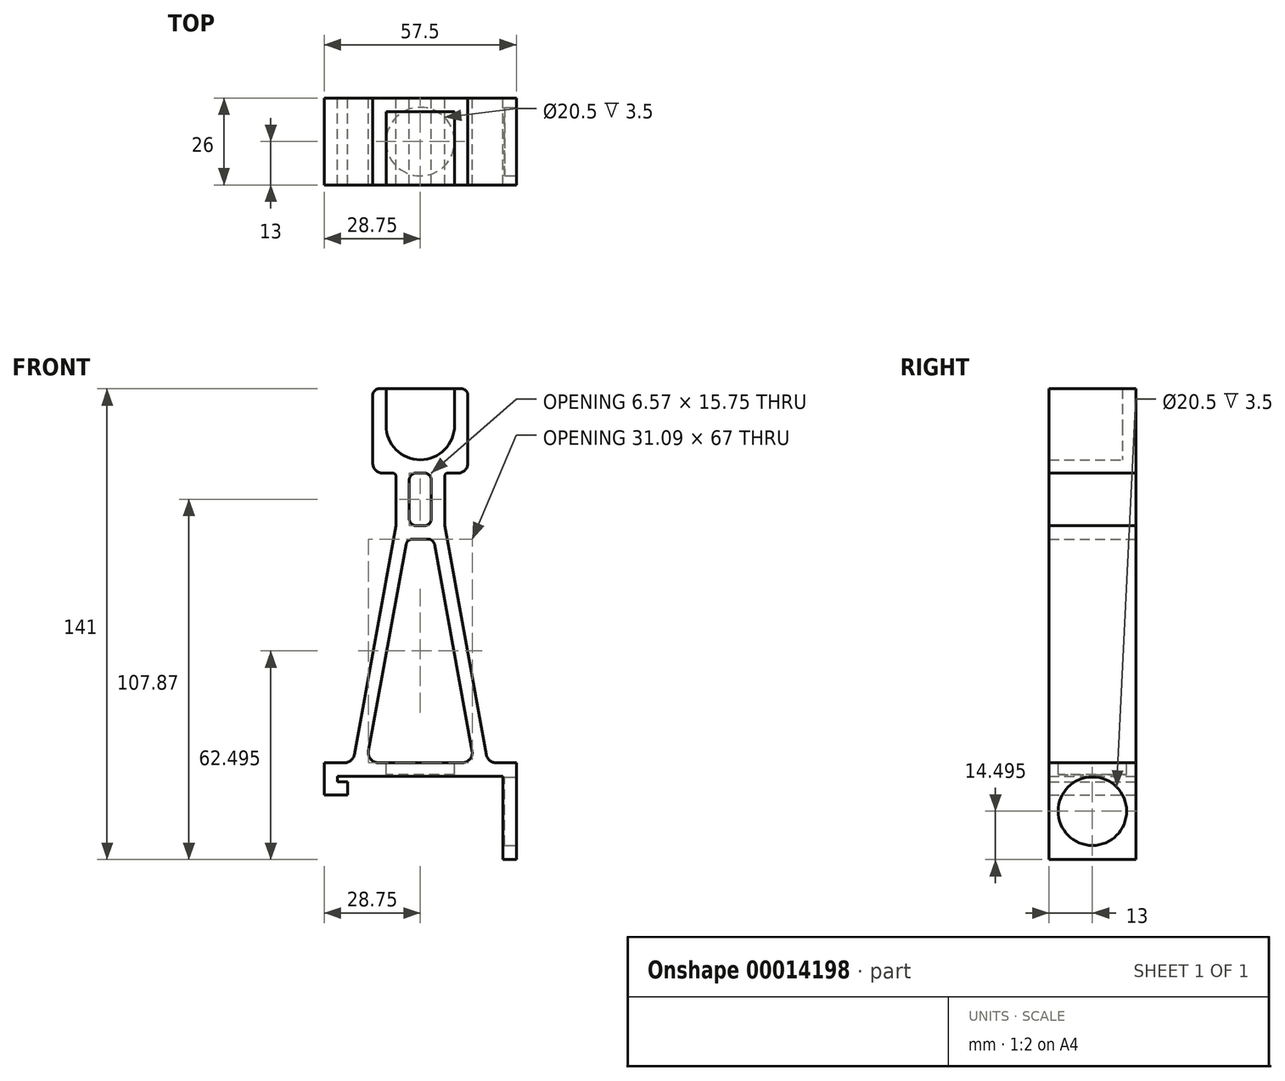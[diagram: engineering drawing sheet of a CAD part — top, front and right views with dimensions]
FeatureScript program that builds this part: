
annotation { "Feature Type Name" : "Feature", "Feature Type Description" : "" }
export const myFeature = defineFeature(function(context is Context, id is Id, definition is map)
    precondition{}
    {
        {
            var Q0;
            Q0=qCreatedBy(makeId("Front.planeOp"),FACE);
            var sketch = newSketch(context, id + "F0", { "sketchPlane" : qUnion([Q0])});
            skLineSegment(sketch, "E0", {"start": v(-28.75, 2.04) * mm, "end": v(-22.71, 2.04) * mm});
            skLineSegment(sketch, "E1", {"start": v(28.75, 2.04) * mm, "end": v(28.75, -26.96) * mm});
            skLineSegment(sketch, "E2", {"start": v(28.75, -26.96) * mm, "end": v(24.75, -26.96) * mm});
            skLineSegment(sketch, "E3", {"start": v(24.75, -26.96) * mm, "end": v(24.75, -1.96) * mm});
            skLineSegment(sketch, "E4", {"start": v(24.75, -1.96) * mm, "end": v(-24.75, -1.96) * mm});
            skLineSegment(sketch, "E5", {"start": v(-24.75, -1.96) * mm, "end": v(-24.75, -3.66) * mm});
            skLineSegment(sketch, "E6", {"start": v(-24.75, -3.66) * mm, "end": v(-21.75, -3.66) * mm});
            skLineSegment(sketch, "E7", {"start": v(-21.75, -3.66) * mm, "end": v(-21.75, -7.66) * mm});
            skLineSegment(sketch, "E8", {"start": v(-21.75, -7.66) * mm, "end": v(-28.75, -7.66) * mm});
            skLineSegment(sketch, "E9", {"start": v(-28.75, -7.66) * mm, "end": v(-28.75, 2.04) * mm});
            skLineSegment(sketch, "E10", {"start": v(-19.76, 4.5) * mm, "end": v(-7.29, 73.04) * mm});
            skLineSegment(sketch, "E11", {"start": v(-1.29, 73.04) * mm, "end": v(1.29, 73.04) * mm});
            skLineSegment(sketch, "E12", {"start": v(7.29, 73.04) * mm, "end": v(19.76, 4.5) * mm});
            skLineSegment(sketch, "E13", {"start": v(-15.5, 5.57) * mm, "end": v(-4.25, 67.4) * mm});
            skLineSegment(sketch, "E14", {"start": v(-2.28, 69.04) * mm, "end": v(2.28, 69.04) * mm});
            skLineSegment(sketch, "E15", {"start": v(4.25, 67.4) * mm, "end": v(15.5, 5.57) * mm});
            skLineSegment(sketch, "E16.trimOffspring", {"start": v(-12.55, 2.04) * mm, "end": v(12.55, 2.04) * mm});
            skLineSegment(sketch, "E17.trimOffspring", {"start": v(22.71, 2.04) * mm, "end": v(28.75, 2.04) * mm});
            skLineSegment(sketch, "E18", {"start": v(-7.29, 73.04) * mm, "end": v(-7.29, 87.79) * mm});
            skLineSegment(sketch, "E19", {"start": v(7.29, 87.79) * mm, "end": v(7.29, 73.04) * mm});
            skLineSegment(sketch, "E20", {"start": v(-3.29, 75.04) * mm, "end": v(-3.29, 86.79) * mm});
            skLineSegment(sketch, "E21", {"start": v(3.29, 86.79) * mm, "end": v(3.29, 75.04) * mm});
            skArc(sketch, "E22", {"start": v(-10.25, 103.04) * mm, "mid": v(0, 92.79) * mm, "end": v(10.25, 103.04) * mm});
            skPoint(sketch, "E22.centerSnap0", {"position": v(0, 73.04) * mm});
            skLineSegment(sketch, "E23", {"start": v(-10.25, 114.04) * mm, "end": v(-10.25, 103.04) * mm});
            skLineSegment(sketch, "E24", {"start": v(10.25, 114.04) * mm, "end": v(10.25, 103.04) * mm});
            skLineSegment(sketch, "E25", {"start": v(-10.25, 114.04) * mm, "end": v(-12.25, 114.04) * mm});
            skLineSegment(sketch, "E26", {"start": v(-14.25, 112.04) * mm, "end": v(-14.25, 91.79) * mm});
            skLineSegment(sketch, "E27", {"start": v(-11.25, 88.79) * mm, "end": v(-8.29, 88.79) * mm});
            skLineSegment(sketch, "E28", {"start": v(14.25, 91.79) * mm, "end": v(14.25, 112.04) * mm});
            skLineSegment(sketch, "E29", {"start": v(12.25, 114.04) * mm, "end": v(10.25, 114.04) * mm});
            skLineSegment(sketch, "E30.trimOffspring", {"start": v(-1.29, 88.79) * mm, "end": v(1.29, 88.79) * mm});
            skLineSegment(sketch, "E31.trimOffspring", {"start": v(8.29, 88.79) * mm, "end": v(11.25, 88.79) * mm});
            skLineSegment(sketch, "E32", {"start": v(-10.25, 114.04) * mm, "end": v(10.25, 114.04) * mm});
            skPoint(sketch, "E33.visualSharp", {"position": v(-14.25, 88.79) * mm});
            skArc(sketch, "E33.filletArc", {"start": v(-14.25, 91.79) * mm, "mid": v(-13.37, 89.66) * mm, "end": v(-11.25, 88.79) * mm});
            skPoint(sketch, "E34.visualSharp", {"position": v(14.25, 88.79) * mm});
            skArc(sketch, "E34.filletArc", {"start": v(11.25, 88.79) * mm, "mid": v(13.37, 89.66) * mm, "end": v(14.25, 91.79) * mm});
            skPoint(sketch, "E35.visualSharp", {"position": v(14.25, 114.04) * mm});
            skArc(sketch, "E35.filletArc", {"start": v(14.25, 112.04) * mm, "mid": v(13.66, 113.45) * mm, "end": v(12.25, 114.04) * mm});
            skPoint(sketch, "E36.visualSharp", {"position": v(-14.25, 114.04) * mm});
            skArc(sketch, "E36.filletArc", {"start": v(-12.25, 114.04) * mm, "mid": v(-13.66, 113.45) * mm, "end": v(-14.25, 112.04) * mm});
            skPoint(sketch, "E37.visualSharp", {"position": v(-7.29, 88.79) * mm});
            skArc(sketch, "E37.filletArc", {"start": v(-7.29, 87.79) * mm, "mid": v(-7.58, 88.5) * mm, "end": v(-8.29, 88.79) * mm});
            skPoint(sketch, "E38.visualSharp", {"position": v(7.29, 88.79) * mm});
            skArc(sketch, "E38.filletArc", {"start": v(8.29, 88.79) * mm, "mid": v(7.58, 88.5) * mm, "end": v(7.29, 87.79) * mm});
            skPoint(sketch, "E39.visualSharp", {"position": v(-3.29, 88.79) * mm});
            skArc(sketch, "E39.filletArc", {"start": v(-1.29, 88.79) * mm, "mid": v(-2.7, 88.2) * mm, "end": v(-3.29, 86.79) * mm});
            skPoint(sketch, "E40.visualSharp", {"position": v(3.29, 88.79) * mm});
            skArc(sketch, "E40.filletArc", {"start": v(3.29, 86.79) * mm, "mid": v(2.7, 88.2) * mm, "end": v(1.29, 88.79) * mm});
            skPoint(sketch, "E41.visualSharp", {"position": v(-3.29, 73.04) * mm});
            skArc(sketch, "E41.filletArc", {"start": v(-3.29, 75.04) * mm, "mid": v(-2.7, 73.62) * mm, "end": v(-1.29, 73.04) * mm});
            skPoint(sketch, "E42.visualSharp", {"position": v(3.29, 73.04) * mm});
            skArc(sketch, "E42.filletArc", {"start": v(1.29, 73.04) * mm, "mid": v(2.7, 73.62) * mm, "end": v(3.29, 75.04) * mm});
            skPoint(sketch, "E43.visualSharp", {"position": v(-3.95, 69.04) * mm});
            skArc(sketch, "E43.filletArc", {"start": v(-2.28, 69.04) * mm, "mid": v(-3.56, 68.57) * mm, "end": v(-4.25, 67.4) * mm});
            skPoint(sketch, "E44.visualSharp", {"position": v(3.95, 69.04) * mm});
            skArc(sketch, "E44.filletArc", {"start": v(4.25, 67.4) * mm, "mid": v(3.56, 68.57) * mm, "end": v(2.28, 69.04) * mm});
            skPoint(sketch, "E45.visualSharp", {"position": v(16.14, 2.04) * mm});
            skArc(sketch, "E45.filletArc", {"start": v(12.55, 2.04) * mm, "mid": v(14.85, 3.11) * mm, "end": v(15.5, 5.57) * mm});
            skPoint(sketch, "E46.visualSharp", {"position": v(-16.14, 2.04) * mm});
            skArc(sketch, "E46.filletArc", {"start": v(-15.5, 5.57) * mm, "mid": v(-14.85, 3.11) * mm, "end": v(-12.55, 2.04) * mm});
            skPoint(sketch, "E47.visualSharp", {"position": v(20.2, 2.04) * mm});
            skArc(sketch, "E47.filletArc", {"start": v(19.76, 4.5) * mm, "mid": v(20.79, 2.73) * mm, "end": v(22.71, 2.04) * mm});
            skPoint(sketch, "E48.visualSharp", {"position": v(-20.2, 2.04) * mm});
            skArc(sketch, "E48.filletArc", {"start": v(-22.71, 2.04) * mm, "mid": v(-20.79, 2.73) * mm, "end": v(-19.76, 4.5) * mm});
            skSolve(sketch);
        }
        {
            var Q0;
            Q0=makeQuery(id+"F0.imprint","IMPRINT",FACE,{"disambiguationData":[TD([[makeQuery(id+"F0.imprint","IMPRINT",EDGE,{"derivedFrom":sQuery(id+"F0.wireOp",EDGE,"E0")}),-1.0]])]});
            extrude(context, id + "F1", {"entities" : qUnion([Q0]), "depth" : 26 * mm});
        }
        {
            var Q0;
            Q0=makeQuery(id+"F1.opExtrude","SWEPT_FACE",FACE,{"disambiguationData":[OSD([sQuery(id+"F0.wireOp",EDGE,"E1")])]});
            var sketch = newSketch(context, id + "F2", { "sketchPlane" : qUnion([Q0])});
            skCircle(sketch, "E49", {"center": v(-13, -12.46) * mm, "radius": 10.25 * mm});
            skPoint(sketch, "E49.centerSnap0", {"position": v(-13, -26.96) * mm});
            skPoint(sketch, "E49.centerSnap1", {"position": v(-26, -12.46) * mm});
            skSolve(sketch);
        }
        {
            var Q0;
            Q0=makeQuery(id+"F2.imprint","IMPRINT",FACE,{"disambiguationData":[TD([[makeQuery(id+"F2.imprint","IMPRINT",EDGE,{"derivedFrom":sQuery(id+"F2.wireOp",EDGE,"E49")}),1.0]])]});
            extrude(context, id + "F3", {"entities" : qUnion([Q0]), "operationType" : NewBodyOperationType.REMOVE, "oppositeDirection" : true, "depth" : 3.5 * mm});
        }
        {
            var Q0;
            Q0=makeQuery(id+"F1.opExtrude","SWEPT_FACE",FACE,{"disambiguationData":[OSD([sQuery(id+"F0.wireOp",EDGE,"E0")])]});
            var sketch = newSketch(context, id + "F4", { "sketchPlane" : qUnion([Q0])});
            skCircle(sketch, "E50", {"center": v(0, -13) * mm, "radius": 10.25 * mm});
            skPoint(sketch, "E50.centerSnap0", {"position": v(-28.75, -13) * mm});
            skSolve(sketch);
        }
        {
            var Q0;
            Q0=makeQuery(id+"F4.imprint","IMPRINT",FACE,{"disambiguationData":[TD([[makeQuery(id+"F4.imprint","IMPRINT",EDGE,{"derivedFrom":sQuery(id+"F4.wireOp",EDGE,"E50")}),1.0]])]});
            extrude(context, id + "F5", {"entities" : qUnion([Q0]), "operationType" : NewBodyOperationType.REMOVE, "oppositeDirection" : true, "depth" : 3.5 * mm});
        }
        {
            var Q0;
            Q0=makeQuery(id+"F0.imprint","IMPRINT",FACE,{"disambiguationData":[TD([[makeQuery(id+"F0.imprint","IMPRINT",EDGE,{"derivedFrom":sQuery(id+"F0.wireOp",EDGE,"E22")}),1.0]])]});
            extrude(context, id + "F6", {"entities" : qUnion([Q0]), "operationType" : NewBodyOperationType.ADD, "depth" : 4 * mm});
        }
    });
